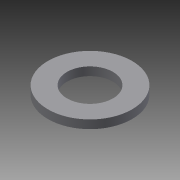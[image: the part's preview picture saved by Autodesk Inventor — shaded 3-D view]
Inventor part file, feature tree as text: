
AUTODESK INVENTOR PART (.ipt)
format: ipt  version: 2013 (Build 170138000, 138)  size: 72,704 bytes
history: native  units: mm
features: extrude x1, sketch x1
ambient origin geometry x8: Origin, YZ Plane, XZ Plane, XY Plane, X Axis, Y Axis, Z Axis, Center Point
bodies: Solid1 (feature_tree)
feature tree (2):
  extrude  "Extrusion1"  Depth=15.0mm
  sketch  "Sketch1"  dims[d0=8.2mm d2=15.0mm d3=1.5mm d4=0.0mm]
